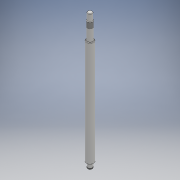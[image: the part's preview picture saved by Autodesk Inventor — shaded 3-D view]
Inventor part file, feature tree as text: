
AUTODESK INVENTOR PART (.ipt)
format: ipt  version: 2018 (Build 220112000, 112)  size: 125,952 bytes
history: native  units: mm
features: extrude x6, sketch x6, other x1, thread x1, chamfer x1
ambient origin geometry x8: Origin, YZ Plane, XZ Plane, XY Plane, X Axis, Y Axis, Z Axis, Center Point
bodies: Body1 (feature_tree)
feature tree (15):
  other  "Sólido1"
  extrude  "Extrusão1"  Depth=235.0mm TaperAngle=0.0deg
  extrude  "Extrusão2"  Depth=39.0mm TaperAngle=0.0deg
  extrude  "Extrusão3"  Depth=10.0mm TaperAngle=0.0deg
  extrude  "Extrusão4"  Depth=9.15mm TaperAngle=0.0deg
  extrude  "Extrusão5"  Depth=1.15mm TaperAngle=0.0deg
  extrude  "Extrusão6"  Depth=1.85mm TaperAngle=0.0deg
  thread  "Rosca1"  [1 undecoded]
  chamfer  "Chanfro1"  Distance=1.0mm Angle=45.0deg
  sketch  "Esboço1"  dims[d0=16.0mm d1=235.0mm d2=0.0mm]
  sketch  "Esboço2"  dims[d3=12.0mm d4=39.0mm d5=0.0mm]
  sketch  "Esboço3"  dims[d6=10.0mm d7=15.0mm d8=0.0mm]
  sketch  "Esboço4"  dims[d9=10.0mm d10=9.15mm d11=0.0mm]
  sketch  "Esboço5"  dims[d12=9.0mm d13=1.15mm d14=0.0mm]
  sketch  "Esboço6"  dims[d15=10.0mm d16=1.85mm d17=0.0mm d18=14.0mm d19=0.0mm d20=1.0mm d21=2.0mm d22=45.0deg]
note: 1 required parameter value undecoded (feature->parameter linkage not recoverable at this tier; creation-order binding heuristic only, values carry confidence <= 0.55)
